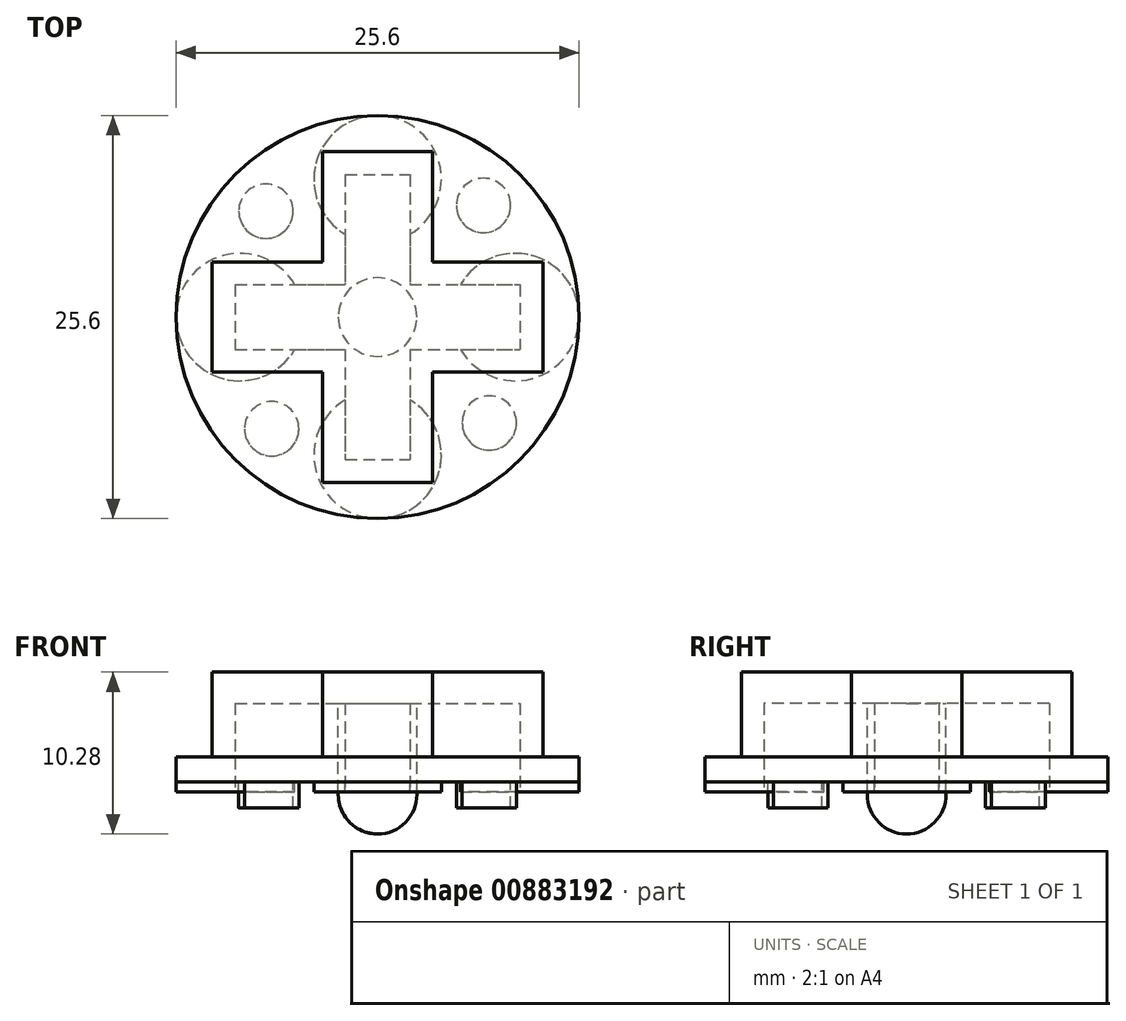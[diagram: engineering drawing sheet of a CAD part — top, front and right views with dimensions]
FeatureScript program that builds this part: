
annotation { "Feature Type Name" : "Feature", "Feature Type Description" : "" }
export const myFeature = defineFeature(function(context is Context, id is Id, definition is map)
    precondition{}
    {
        {
            var Q0;
            Q0=qCreatedBy(makeId("Top.planeOp"),FACE);
            var sketch = newSketch(context, id + "F0", { "sketchPlane" : qUnion([Q0])});
            skCircle(sketch, "E0", {"center": v(0, 0) * mm, "radius": 12.8 * mm});
            skSolve(sketch);
        }
        {
            var Q0;
            Q0=makeQuery(id+"F0.imprint","IMPRINT",FACE,{"disambiguationData":[TD([[makeQuery(id+"F0.imprint","IMPRINT",EDGE,{"derivedFrom":sQuery(id+"F0.wireOp",EDGE,"E0")}),1.0]])]});
            extrude(context, id + "F1", {"entities" : qUnion([Q0]), "depth" : 1.6 * mm, "offsetDistance" : 25 * mm});
        }
        {
            var Q0;
            Q0=makeQuery(id+"F1.opExtrude","CAP_FACE",FACE,{"disambiguationData":[OSD([sQuery(id+"F0.wireOp",EDGE,"E0")])],"isStart":false});
            var sketch = newSketch(context, id + "F2", { "sketchPlane" : qUnion([Q0])});
            skLineSegment(sketch, "E1.bottom", {"start": v(3.5, 10.5) * mm, "end": v(-3.5, 10.5) * mm});
            skLineSegment(sketch, "E1.top", {"start": v(3.5, -10.5) * mm, "end": v(-3.5, -10.5) * mm});
            skLineSegment(sketch, "E1.left", {"start": v(3.5, 10.5) * mm, "end": v(3.5, -10.5) * mm});
            skLineSegment(sketch, "E1.right", {"start": v(-3.5, 10.5) * mm, "end": v(-3.5, -10.5) * mm});
            skPoint(sketch, "E1.middle", {"position": v(0, 0) * mm});
            skLineSegment(sketch, "E2.bottom", {"start": v(10.5, 3.5) * mm, "end": v(-10.5, 3.5) * mm});
            skLineSegment(sketch, "E2.top", {"start": v(10.5, -3.5) * mm, "end": v(-10.5, -3.5) * mm});
            skLineSegment(sketch, "E2.left", {"start": v(10.5, 3.5) * mm, "end": v(10.5, -3.5) * mm});
            skLineSegment(sketch, "E2.right", {"start": v(-10.5, 3.5) * mm, "end": v(-10.5, -3.5) * mm});
            skSolve(sketch);
        }
        {
            var Q0;
            Q0 = qSketchRegion(id + "F2", true);
            extrude(context, id + "F3", {"entities" : qUnion([Q0]), "operationType" : NewBodyOperationType.ADD, "depth" : 5.38 * mm, "offsetDistance" : 25 * mm});
        }
        {
            var Q0;
            Q0=makeQuery(id+"F1.opExtrude","CAP_FACE",FACE,{"disambiguationData":[OSD([sQuery(id+"F0.wireOp",EDGE,"E0")])],"isStart":true});
            var sketch = newSketch(context, id + "F4", { "sketchPlane" : qUnion([Q0])});
            skLineSegment(sketch, "E3.bottom", {"start": v(-2.06, -9.05) * mm, "end": v(2.06, -9.05) * mm});
            skLineSegment(sketch, "E3.top", {"start": v(-2.06, 9.05) * mm, "end": v(2.06, 9.05) * mm});
            skLineSegment(sketch, "E3.left", {"start": v(-2.06, -9.05) * mm, "end": v(-2.06, 9.05) * mm});
            skLineSegment(sketch, "E3.right", {"start": v(2.06, -9.05) * mm, "end": v(2.06, 9.05) * mm});
            skPoint(sketch, "E3.middle", {"position": v(0, 0) * mm});
            skLineSegment(sketch, "E4.bottom", {"start": v(-9.05, -2.06) * mm, "end": v(9.05, -2.06) * mm});
            skLineSegment(sketch, "E4.top", {"start": v(-9.05, 2.05) * mm, "end": v(9.05, 2.06) * mm});
            skLineSegment(sketch, "E4.left", {"start": v(-9.05, -2.06) * mm, "end": v(-9.05, 2.06) * mm});
            skLineSegment(sketch, "E4.right", {"start": v(9.05, -2.06) * mm, "end": v(9.05, 2.06) * mm});
            skSolve(sketch);
        }
        {
            var Q0;
            Q0 = qSketchRegion(id + "F4", true);
            extrude(context, id + "F5", {"entities" : qUnion([Q0]), "operationType" : NewBodyOperationType.REMOVE, "oppositeDirection" : true, "depth" : 5 * mm, "offsetDistance" : 25 * mm});
        }
        {
            var Q0;
            Q0=makeQuery(id+"F5.boolean.opBoolean","COPY",FACE,{"derivedFrom":makeQuery(id+"F5.opExtrude","CAP_FACE",FACE,{"disambiguationData":[OSD([sQuery(id+"F4.wireOp",EDGE,"E3.bottom"),sQuery(id+"F4.wireOp",EDGE,"E3.top"),sQuery(id+"F4.wireOp",EDGE,"E3.left"),sQuery(id+"F4.wireOp",EDGE,"E3.right"),sQuery(id+"F4.wireOp",EDGE,"E4.bottom"),sQuery(id+"F4.wireOp",EDGE,"E4.top"),sQuery(id+"F4.wireOp",EDGE,"E4.left"),sQuery(id+"F4.wireOp",EDGE,"E4.right")])],"isStart":false})});
            var sketch = newSketch(context, id + "F6", { "sketchPlane" : qUnion([Q0])});
            skCircle(sketch, "E5", {"center": v(0, 0) * mm, "radius": 2.5 * mm});
            skSolve(sketch);
        }
        {
            var Q0;
            Q0 = qSketchRegion(id + "F6", true);
            extrude(context, id + "F7", {"entities" : qUnion([Q0]), "operationType" : NewBodyOperationType.ADD, "depth" : 8.3 * mm, "offsetDistance" : 25 * mm});
        }
        {
            var Q0;
            Q0=makeQuery(id+"F1.opExtrude","CAP_FACE",FACE,{"disambiguationData":[OSD([sQuery(id+"F0.wireOp",EDGE,"E0")])],"isStart":true});
            var sketch = newSketch(context, id + "F8", { "sketchPlane" : qUnion([Q0])});
            skCircle(sketch, "E6", {"center": v(0, 8.75) * mm, "radius": 4.05 * mm});
            skPoint(sketch, "E7", {"position": v(0, 9.05) * mm});
            skCircle(sketch, "E8.1.0", {"center": v(-8.75, 0) * mm, "radius": 4.05 * mm});
            skCircle(sketch, "E8.2.0", {"center": v(0, -8.75) * mm, "radius": 4.05 * mm});
            skCircle(sketch, "E8.3.0", {"center": v(8.75, 0) * mm, "radius": 4.05 * mm});
            skPoint(sketch, "E8.center", {"position": v(0, 0) * mm});
            skLineSegment(sketch, "E9.bottom", {"start": v(-2.06, 9.05) * mm, "end": v(2.06, 9.05) * mm});
            skLineSegment(sketch, "E9.top", {"start": v(-2.06, -9.05) * mm, "end": v(2.06, -9.05) * mm});
            skLineSegment(sketch, "E9.left", {"start": v(-2.06, 9.05) * mm, "end": v(-2.06, -9.05) * mm});
            skLineSegment(sketch, "E9.right", {"start": v(2.06, 9.05) * mm, "end": v(2.06, -9.05) * mm});
            skLineSegment(sketch, "E10.bottom", {"start": v(9.05, 2.06) * mm, "end": v(-9.05, 2.06) * mm});
            skLineSegment(sketch, "E10.top", {"start": v(9.05, -2.06) * mm, "end": v(-9.05, -2.06) * mm});
            skLineSegment(sketch, "E10.left", {"start": v(9.05, 2.06) * mm, "end": v(9.05, -2.06) * mm});
            skLineSegment(sketch, "E10.right", {"start": v(-9.05, 2.06) * mm, "end": v(-9.05, -2.06) * mm});
            skSolve(sketch);
        }
        {
            var Q0;
            {var subQ0=sQuery(id+"F8.wireOp",EDGE,"E10.right");Q0=makeQuery(id+"F8.imprint","IMPRINT",FACE,{"disambiguationData":[TD([[makeQuery(id+"F8.imprint","IMPRINT",EDGE,{"derivedFrom":subQ0}),1.0]])]});}
            var Q1;
            {var subQ1=sQuery(id+"F8.wireOp",EDGE,"E9.bottom");Q1=makeQuery(id+"F8.imprint","IMPRINT",FACE,{"disambiguationData":[TD([[makeQuery(id+"F8.imprint","IMPRINT",EDGE,{"derivedFrom":subQ1}),1.0]])]});}
            var Q2;
            {var subQ0=sQuery(id+"F8.wireOp",EDGE,"E10.left");Q2=makeQuery(id+"F8.imprint","IMPRINT",FACE,{"disambiguationData":[TD([[makeQuery(id+"F8.imprint","IMPRINT",EDGE,{"derivedFrom":subQ0}),-1.0]])]});}
            var Q3;
            {var subQ1=sQuery(id+"F8.wireOp",EDGE,"E9.top");Q3=makeQuery(id+"F8.imprint","IMPRINT",FACE,{"disambiguationData":[TD([[makeQuery(id+"F8.imprint","IMPRINT",EDGE,{"derivedFrom":subQ1}),-1.0]])]});}
            extrude(context, id + "F9", {"entities" : qUnion([Q0, Q1, Q2, Q3]), "operationType" : NewBodyOperationType.ADD, "depth" : 0.63 * mm, "offsetDistance" : 25 * mm});
        }
        {
            var Q0;
            {var subQ1=sQuery(id+"F4.wireOp",EDGE,"E3.left");var subQ4=sQuery(id+"F0.wireOp",EDGE,"E0");var subQ5=makeQuery(id+"F1.opExtrude","CAP_FACE",FACE,{"disambiguationData":[OSD([subQ4])],"isStart":true});Q0=makeQuery(id+"F9.boolean.opBoolean","SPLIT",FACE,{"disambiguationData":[TD([makeQuery(id+"F5.boolean.opBoolean","COPY",FACE,{"derivedFrom":makeQuery(id+"F5.opExtrude","SWEPT_FACE",FACE,{"disambiguationData":[OSD([subQ1]),TDD([makeQuery(id+"F4.imprint","IMPRINT",EDGE,{"disambiguationData":[TD([[makeQuery(id+"F4.imprint","INTERSECT",VERTEX,{"derivedFrom":[sQuery(id+"F4.wireOp",EDGE,"E3.top"),subQ1]}),1.0]])],"derivedFrom":subQ1})])]})})])],"derivedFrom":subQ5});}
            var sketch = newSketch(context, id + "F10", { "sketchPlane" : qUnion([Q0])});
            skCircle(sketch, "E11", {"center": v(-6.72, 7.1) * mm, "radius": 1.73 * mm});
            skCircle(sketch, "E12", {"center": v(0, 0) * mm, "radius": 11.5 * mm});
            skCircle(sketch, "E13.1.0", {"center": v(-7.1, -6.72) * mm, "radius": 1.73 * mm});
            skCircle(sketch, "E13.2.0", {"center": v(6.72, -7.1) * mm, "radius": 1.73 * mm});
            skCircle(sketch, "E13.3.0", {"center": v(7.1, 6.72) * mm, "radius": 1.73 * mm});
            skSolve(sketch);
        }
        {
            var Q0;
            Q0=makeQuery(id+"F10.imprint","IMPRINT",FACE,{"disambiguationData":[TD([[makeQuery(id+"F10.imprint","IMPRINT",EDGE,{"derivedFrom":sQuery(id+"F10.wireOp",EDGE,"E11")}),1.0]])]});
            var Q1;
            Q1=makeQuery(id+"F10.imprint","IMPRINT",FACE,{"disambiguationData":[TD([[makeQuery(id+"F10.imprint","IMPRINT",EDGE,{"derivedFrom":sQuery(id+"F10.wireOp",EDGE,"E13.1.0")}),1.0]])]});
            var Q2;
            Q2=makeQuery(id+"F10.imprint","IMPRINT",FACE,{"disambiguationData":[TD([[makeQuery(id+"F10.imprint","IMPRINT",EDGE,{"derivedFrom":sQuery(id+"F10.wireOp",EDGE,"E13.2.0")}),1.0]])]});
            var Q3;
            Q3=makeQuery(id+"F10.imprint","IMPRINT",FACE,{"disambiguationData":[TD([[makeQuery(id+"F10.imprint","IMPRINT",EDGE,{"derivedFrom":sQuery(id+"F10.wireOp",EDGE,"E13.3.0")}),1.0]])]});
            extrude(context, id + "F11", {"entities" : qUnion([Q0, Q1, Q2, Q3]), "operationType" : NewBodyOperationType.ADD, "depth" : 1.65 * mm, "offsetDistance" : 25 * mm});
        }
        {
            var Q0;
            Q0=makeQuery(id+"F7.opExtrude","CAP_EDGE",EDGE,{"disambiguationData":[OSD([sQuery(id+"F6.wireOp",EDGE,"E5")])],"isStart":false});
            fillet(context, id + "F12", {"entities" : qUnion([Q0]), "radius" : 2.5 * mm, "tangentPropagation" : true, "allowEdgeOverflow" : false});
        }
    });
